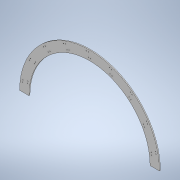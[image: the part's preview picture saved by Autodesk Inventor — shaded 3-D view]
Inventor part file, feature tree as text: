
AUTODESK INVENTOR PART (.ipt)
format: ipt  version: 2020.3 (Build 243373000, 373)  size: 168,448 bytes
history: native  units: mm
features: extrude x3, sketch x3, pattern_circular x1
ambient origin geometry x8: Origin, YZ Plane, XZ Plane, XY Plane, X Axis, Y Axis, Z Axis, Center Point
bodies: Solid1 (feature_tree)
feature tree (7):
  extrude  "Extrusion1"  Depth=40.0mm
  extrude  "Extrusion2"  Depth=10.0mm TaperAngle=0.0deg
  extrude  "Extrusion3"  Depth=3.0mm
  pattern_circular  "Circular Pattern1"  Count=27  [1 undecoded]
  sketch  "Sketch1"  dims[d0=600.0mm d1=40.0mm]
  sketch  "Sketch2"  dims[d2=4.0mm d3=0.0mm d4=10.0mm d5=0.0mm]
  sketch  "Sketch3"  dims[d6=3.0mm d7=3.0mm d9=270.0mm d11=3.0mm d12=3.0mm d14=270.0mm d16=0.0mm d17=0.0mm d18=90.0mm d19=27.925268mm d21=20.071286mm d22=20.0mm d23=1.570796mm d24=1.919862mm]
note: 1 required parameter value undecoded (feature->parameter linkage not recoverable at this tier; creation-order binding heuristic only, values carry confidence <= 0.55)
